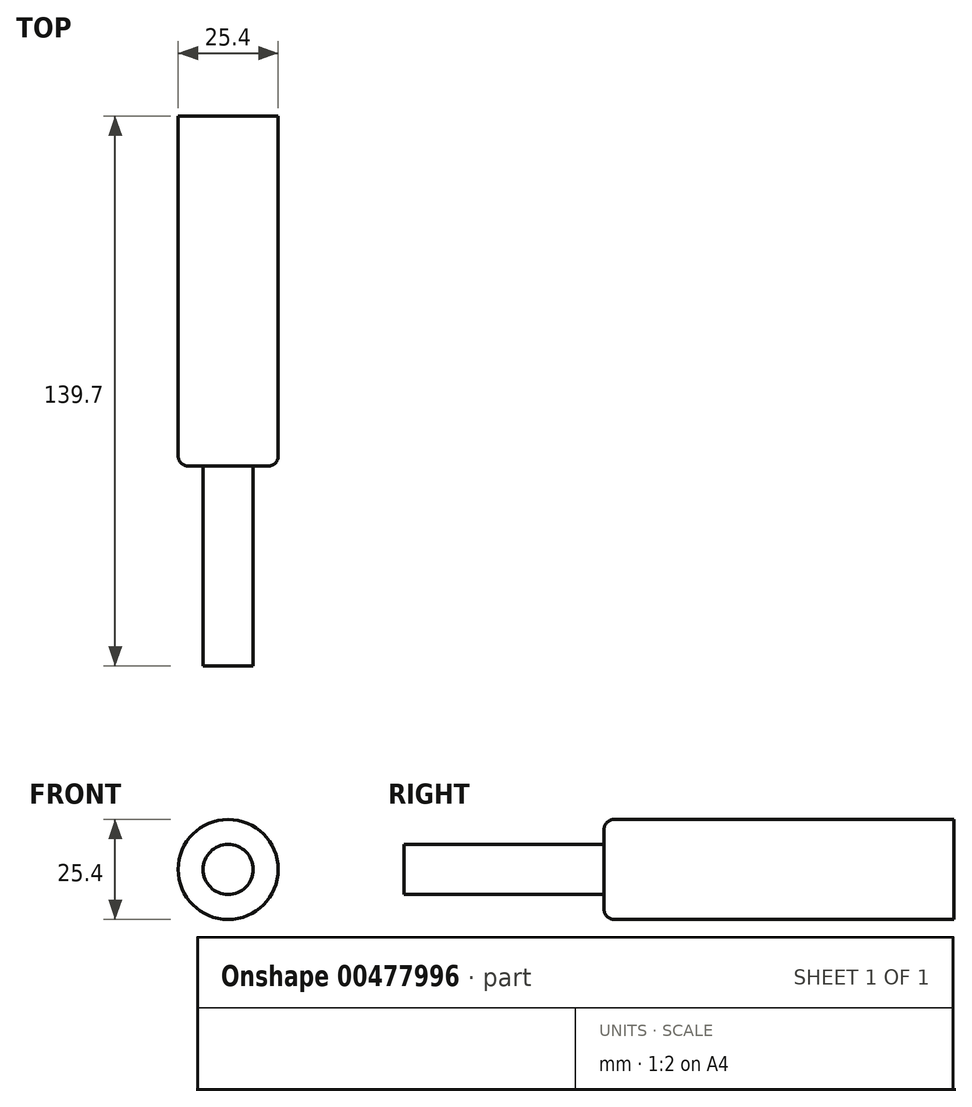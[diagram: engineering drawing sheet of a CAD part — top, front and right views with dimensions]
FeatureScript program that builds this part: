
annotation { "Feature Type Name" : "Feature", "Feature Type Description" : "" }
export const myFeature = defineFeature(function(context is Context, id is Id, definition is map)
    precondition{}
    {
        {
            var Q0;
            Q0=qCreatedBy(makeId("Front.planeOp"),FACE);
            var sketch = newSketch(context, id + "F0", { "sketchPlane" : qUnion([Q0])});
            skCircle(sketch, "E0", {"center": v(0, 0) * mm, "radius": 12.7 * mm});
            skSolve(sketch);
        }
        {
            var Q0;
            Q0=makeQuery(id+"F0.imprint","IMPRINT",FACE,{"disambiguationData":[TD([[makeQuery(id+"F0.imprint","IMPRINT",EDGE,{"derivedFrom":sQuery(id+"F0.wireOp",EDGE,"E0")}),1.0]])]});
            extrude(context, id + "F1", {"entities" : qUnion([Q0]), "depth" : 88.9 * mm});
        }
        {
            var Q0;
            Q0=makeQuery(id+"F1.opExtrude","CAP_FACE",FACE,{"disambiguationData":[OSD([sQuery(id+"F0.wireOp",EDGE,"E0")])],"isStart":false});
            var sketch = newSketch(context, id + "F2", { "sketchPlane" : qUnion([Q0])});
            skCircle(sketch, "E1", {"center": v(0, 0) * mm, "radius": 6.35 * mm});
            skSolve(sketch);
        }
        {
            var Q0;
            Q0=makeQuery(id+"F2.imprint","IMPRINT",FACE,{"disambiguationData":[TD([[makeQuery(id+"F2.imprint","IMPRINT",EDGE,{"derivedFrom":sQuery(id+"F2.wireOp",EDGE,"E1")}),1.0]])]});
            extrude(context, id + "F3", {"entities" : qUnion([Q0]), "operationType" : NewBodyOperationType.ADD, "depth" : 50.8 * mm});
        }
        {
            var Q0;
            Q0=makeQuery(id+"F1.opExtrude","CAP_EDGE",EDGE,{"disambiguationData":[OSD([sQuery(id+"F0.wireOp",EDGE,"E0")])],"isStart":false});
            fillet(context, id + "F4", {"entities" : qUnion([Q0]), "radius" : 2.54 * mm, "tangentPropagation" : true, "allowEdgeOverflow" : false});
        }
    });
